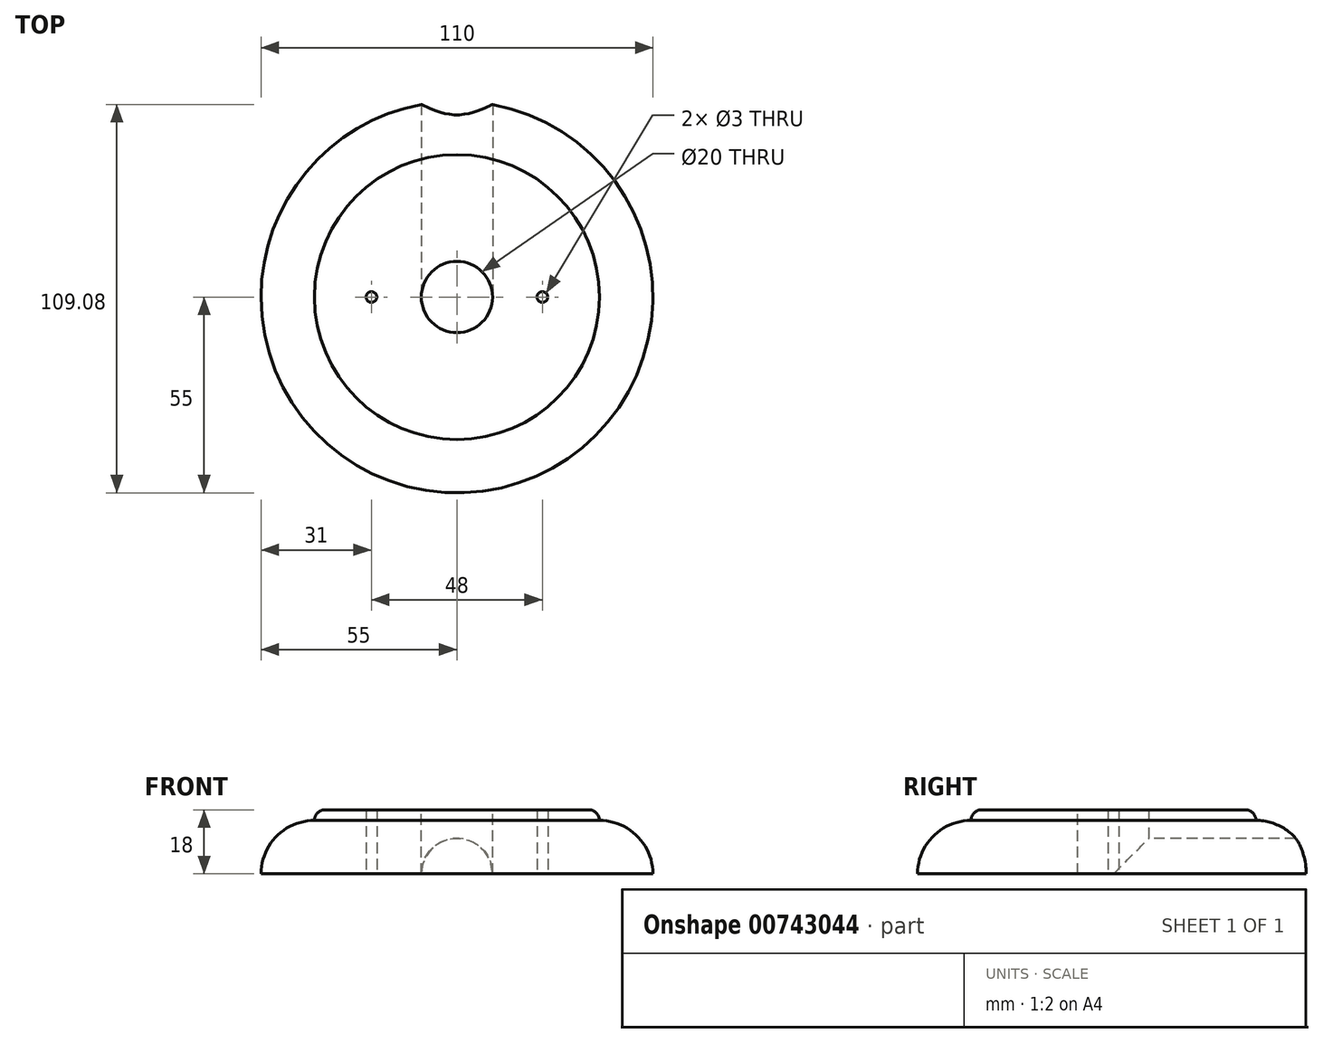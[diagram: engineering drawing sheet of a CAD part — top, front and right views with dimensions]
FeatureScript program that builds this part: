
annotation { "Feature Type Name" : "Feature", "Feature Type Description" : "" }
export const myFeature = defineFeature(function(context is Context, id is Id, definition is map)
    precondition{}
    {
        {
            var Q0;
            Q0=qCreatedBy(makeId("Front.planeOp"),FACE);
            var sketch = newSketch(context, id + "F0", { "sketchPlane" : qUnion([Q0])});
            skLineSegment(sketch, "E0", {"start": v(-55, 0) * mm, "end": v(55, 0) * mm});
            skLineSegment(sketch, "E1", {"start": v(55, 0) * mm, "end": v(55, 15) * mm});
            skLineSegment(sketch, "E2", {"start": v(55, 15) * mm, "end": v(40, 15) * mm});
            skLineSegment(sketch, "E3", {"start": v(40, 15) * mm, "end": v(40, 18) * mm});
            skLineSegment(sketch, "E4", {"start": v(40, 18) * mm, "end": v(-40, 18) * mm});
            skLineSegment(sketch, "E5", {"start": v(-40, 18) * mm, "end": v(-40, 15) * mm});
            skLineSegment(sketch, "E6", {"start": v(-40, 15) * mm, "end": v(-55, 15) * mm});
            skLineSegment(sketch, "E7", {"start": v(-55, 15) * mm, "end": v(-55, 0) * mm});
            skLineSegment(sketch, "E8", {"start": v(0, 0) * mm, "end": v(0, 18) * mm});
            skLineSegment(sketch, "E9", {"start": v(0, 18) * mm, "end": v(0, 43.04) * mm});
            skLineSegment(sketch, "E10", {"start": v(0, 43.04) * mm, "end": v(10, 43.04) * mm});
            skLineSegment(sketch, "E11", {"start": v(10, 43.04) * mm, "end": v(10, -6.96) * mm});
            skLineSegment(sketch, "E12", {"start": v(10, -6.96) * mm, "end": v(0, -6.96) * mm});
            skLineSegment(sketch, "E13", {"start": v(0, -6.96) * mm, "end": v(0, 43.04) * mm});
            skSolve(sketch);
        }
        {
            var Q0;
            {var subQ0=sQuery(id+"F0.wireOp",EDGE,"E5");Q0=makeQuery(id+"F0.imprint","IMPRINT",FACE,{"disambiguationData":[TD([[makeQuery(id+"F0.imprint","IMPRINT",EDGE,{"derivedFrom":subQ0}),1.0]])]});}
            var Q1;
            Q1=sQuery(id+"F0.wireOp",EDGE,"E8");
            revolve(context, id + "F1", {"surfaceOperationType" : NewSurfaceOperationType.NEW, "entities" : qUnion([Q0]), "axis" : qUnion([Q1]), "revolveType" : RevolveType.FULL});
        }
        {
            var Q0;
            {var subQ5=sQuery(id+"F0.wireOp",EDGE,"E10");Q0=makeQuery(id+"F0.imprint","IMPRINT",FACE,{"disambiguationData":[TD([[makeQuery(id+"F0.imprint","IMPRINT",EDGE,{"derivedFrom":subQ5}),-1.0]])]});}
            var Q1;
            {var subQ0=sQuery(id+"F0.wireOp",EDGE,"E13");var subQ1=sQuery(id+"F0.wireOp",EDGE,"E0");var subQ2=makeQuery(id+"F0.imprint","INTERSECT",VERTEX,{"derivedFrom":[subQ1,subQ0]});Q1=makeQuery(id+"F0.imprint","IMPRINT",FACE,{"disambiguationData":[TD([[makeQuery(id+"F0.imprint","IMPRINT",EDGE,{"disambiguationData":[TD([[subQ2,-1.0]])],"derivedFrom":subQ1}),1.0]])]});}
            var Q2;
            {var subQ5=sQuery(id+"F0.wireOp",EDGE,"E12");Q2=makeQuery(id+"F0.imprint","IMPRINT",FACE,{"disambiguationData":[TD([[makeQuery(id+"F0.imprint","IMPRINT",EDGE,{"derivedFrom":subQ5}),-1.0]])]});}
            var Q3;
            Q3=sQuery(id+"F0.wireOp",EDGE,"E13");
            revolve(context, id + "F2", {"operationType" : NewBodyOperationType.REMOVE, "surfaceOperationType" : NewSurfaceOperationType.NEW, "entities" : qUnion([Q0, Q1, Q2]), "axis" : qUnion([Q3]), "revolveType" : RevolveType.FULL, "oppositeDirection" : true});
        }
        {
            var Q0;
            Q0=qCreatedBy(makeId("Front.planeOp"),FACE);
            var sketch = newSketch(context, id + "F3", { "sketchPlane" : qUnion([Q0])});
            skCircle(sketch, "E14", {"center": v(0, 0) * mm, "radius": 10 * mm});
            skSolve(sketch);
        }
        {
            var Q0;
            Q0=makeQuery(id+"F3.imprint","IMPRINT",FACE,{"disambiguationData":[TD([[makeQuery(id+"F3.imprint","IMPRINT",EDGE,{"derivedFrom":sQuery(id+"F3.wireOp",EDGE,"E14")}),1.0]])]});
            extrude(context, id + "F4", {"entities" : qUnion([Q0]), "operationType" : NewBodyOperationType.REMOVE, "oppositeDirection" : true, "depth" : 141.6 * mm, "offsetDistance" : 25 * mm});
        }
        {
            var Q0;
            Q0=makeQuery(id+"F1.opRevolve","SWEPT_EDGE",EDGE,{"disambiguationData":[OSD([sQuery(id+"F0.wireOp",EDGE,"E6"),sQuery(id+"F0.wireOp",EDGE,"E7")])]});
            fillet(context, id + "F5", {"entities" : qUnion([Q0]), "radius" : 15 * mm, "tangentPropagation" : true, "allowEdgeOverflow" : false});
        }
        {
            var Q0;
            Q0=qCreatedBy(makeId("Top.planeOp"),FACE);
            var sketch = newSketch(context, id + "F6", { "sketchPlane" : qUnion([Q0])});
            skPoint(sketch, "E15", {"position": v(24, 0) * mm});
            skPoint(sketch, "E16", {"position": v(-24, 0) * mm});
            skSolve(sketch);
        }
        {
            var Q0;
            Q0=sQuery(id+"F6.wireOp",VERTEX,"E15");
            var Q1;
            Q1=makeQuery(id+"F1.opRevolve","SWEPT_BODY",BODY,{"disambiguationData":[OSD([sQuery(id+"F0.wireOp",EDGE,"E0"),sQuery(id+"F0.wireOp",EDGE,"E4"),sQuery(id+"F0.wireOp",EDGE,"E5"),sQuery(id+"F0.wireOp",EDGE,"E6"),sQuery(id+"F0.wireOp",EDGE,"E7"),sQuery(id+"F0.wireOp",EDGE,"E13")])]});
            hole(context, id + "F7", {"style" : HoleStyle.SIMPLE, "endStyle" : HoleEndStyle.THROUGH, "oppositeDirection" : true, "holeDiameter" : 3 * mm, "majorDiameter" : 5 * mm, "isTappedThrough" : true, "tappedDepth" : 12 * mm, "tapClearance" : 3, "locations" : qUnion([Q0]), "scope" : qUnion([Q1])});
        }
        {
            var Q0;
            Q0=sQuery(id+"F6.wireOp",VERTEX,"E16");
            var Q1;
            Q1=makeQuery(id+"F1.opRevolve","SWEPT_BODY",BODY,{"disambiguationData":[OSD([sQuery(id+"F0.wireOp",EDGE,"E0"),sQuery(id+"F0.wireOp",EDGE,"E4"),sQuery(id+"F0.wireOp",EDGE,"E5"),sQuery(id+"F0.wireOp",EDGE,"E6"),sQuery(id+"F0.wireOp",EDGE,"E7"),sQuery(id+"F0.wireOp",EDGE,"E13")])]});
            hole(context, id + "F8", {"style" : HoleStyle.SIMPLE, "endStyle" : HoleEndStyle.THROUGH, "oppositeDirection" : true, "holeDiameter" : 3 * mm, "majorDiameter" : 5 * mm, "isTappedThrough" : true, "tappedDepth" : 12 * mm, "tapClearance" : 3, "locations" : qUnion([Q0]), "scope" : qUnion([Q1])});
        }
        {
            var Q0;
            Q0=makeQuery(id+"F1.opRevolve","SWEPT_EDGE",EDGE,{"disambiguationData":[OSD([sQuery(id+"F0.wireOp",EDGE,"E4"),sQuery(id+"F0.wireOp",EDGE,"E5")])]});
            fillet(context, id + "F9", {"entities" : qUnion([Q0]), "radius" : 3 * mm, "tangentPropagation" : true, "allowEdgeOverflow" : false});
        }
    });
